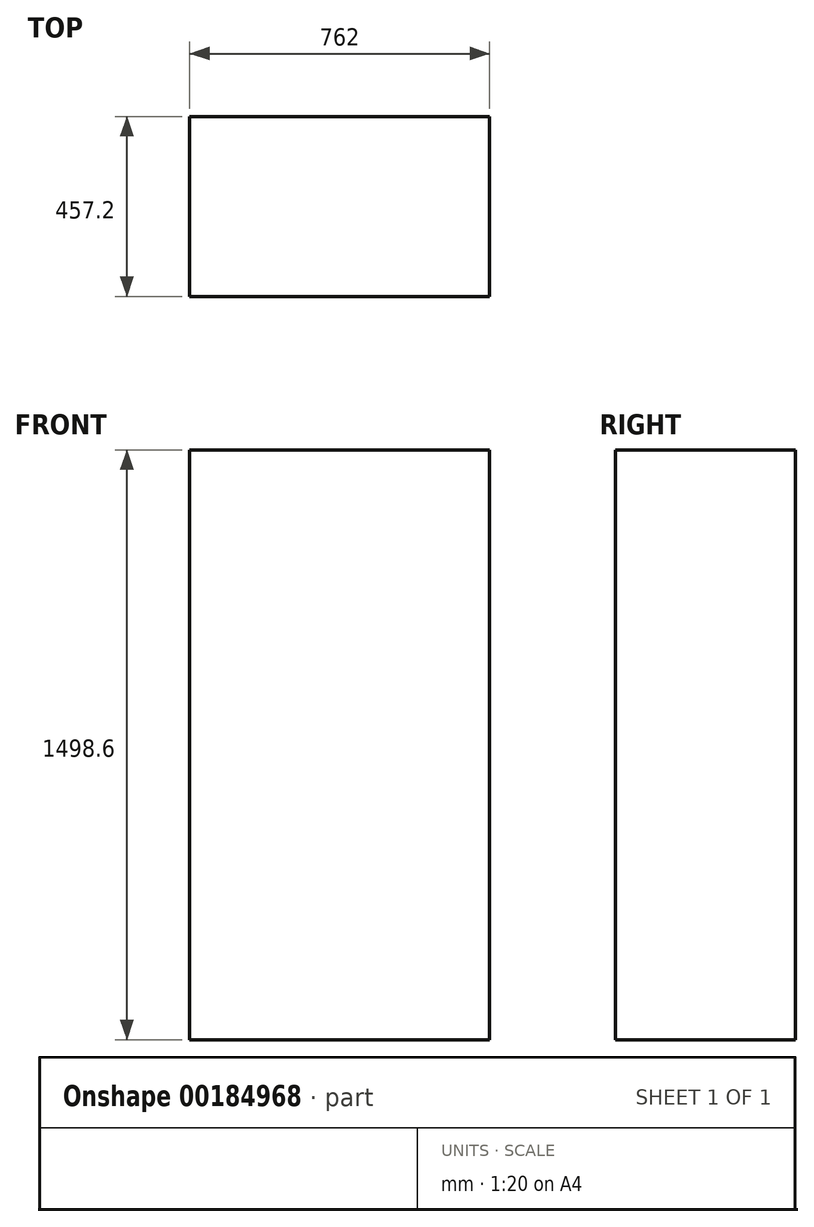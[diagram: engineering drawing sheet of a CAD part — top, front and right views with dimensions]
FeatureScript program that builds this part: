
annotation { "Feature Type Name" : "Feature", "Feature Type Description" : "" }
export const myFeature = defineFeature(function(context is Context, id is Id, definition is map)
    precondition{}
    {
        {
            var Q0;
            Q0=qCreatedBy(makeId("Top.planeOp"),FACE);
            var sketch = newSketch(context, id + "F0", { "sketchPlane" : qUnion([Q0])});
            skLineSegment(sketch, "E0.bottom", {"start": v(381, 228.6) * mm, "end": v(-381, 228.6) * mm});
            skLineSegment(sketch, "E0.top", {"start": v(381, -228.6) * mm, "end": v(-381, -228.6) * mm});
            skLineSegment(sketch, "E0.left", {"start": v(381, 228.6) * mm, "end": v(381, -228.6) * mm});
            skLineSegment(sketch, "E0.right", {"start": v(-381, 228.6) * mm, "end": v(-381, -228.6) * mm});
            skPoint(sketch, "E0.middle", {"position": v(0, 0) * mm});
            skSolve(sketch);
        }
        {
            var Q0;
            Q0=makeQuery(id+"F0.imprint","IMPRINT",FACE,{"disambiguationData":[TD([[makeQuery(id+"F0.imprint","IMPRINT",EDGE,{"derivedFrom":sQuery(id+"F0.wireOp",EDGE,"E0.bottom")}),1.0]])]});
            extrude(context, id + "F1", {"entities" : qUnion([Q0]), "depth" : 1498.6 * mm});
        }
    });
